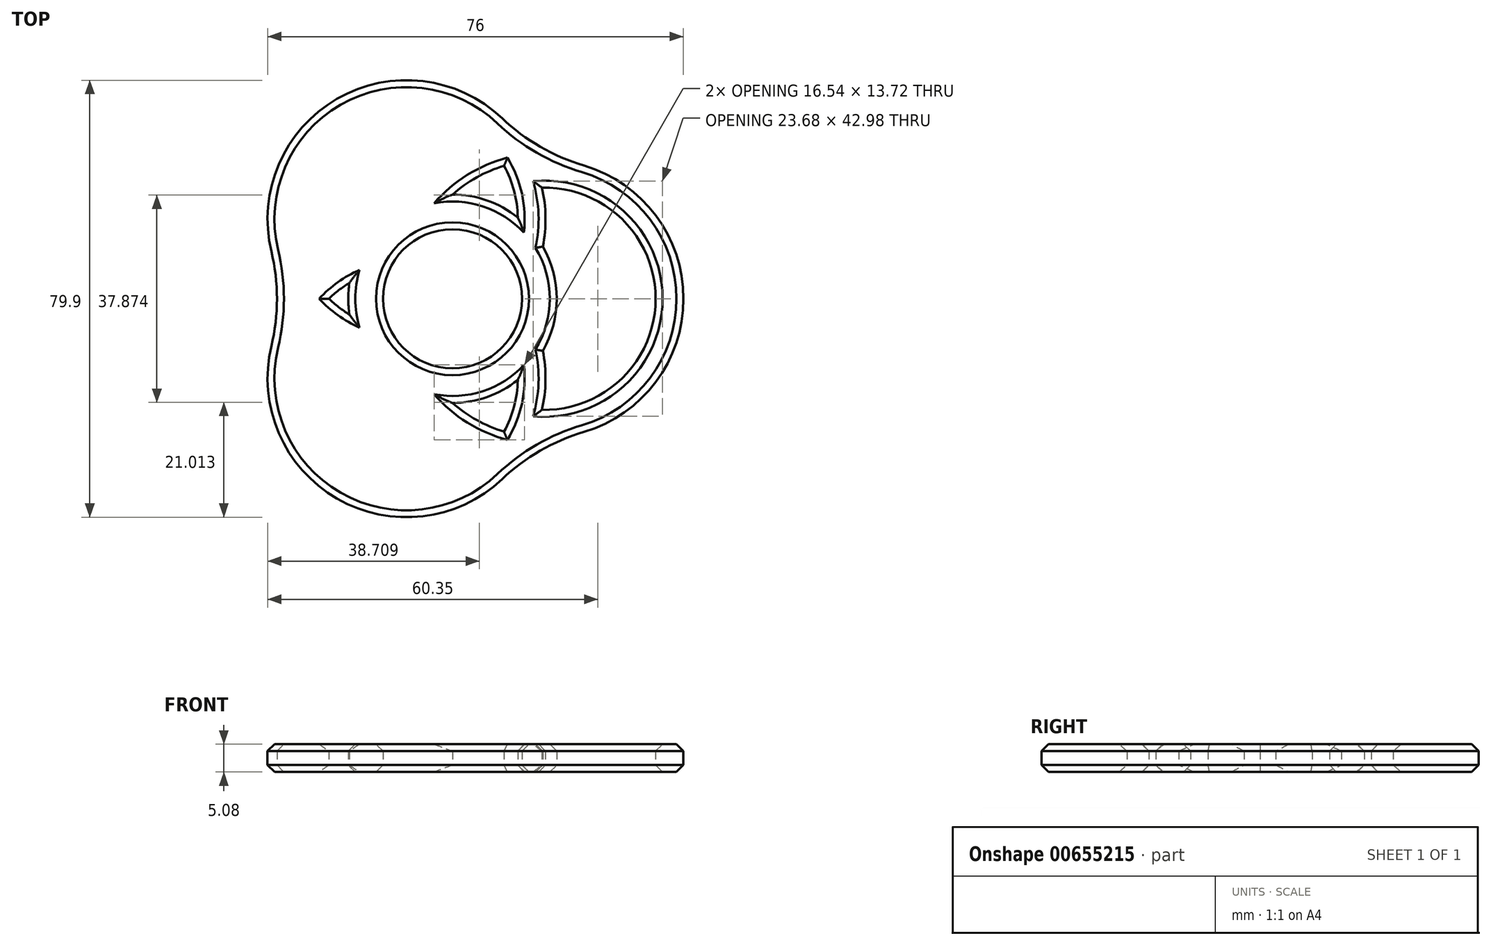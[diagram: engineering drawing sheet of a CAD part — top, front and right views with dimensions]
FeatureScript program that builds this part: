
annotation { "Feature Type Name" : "Feature", "Feature Type Description" : "" }
export const myFeature = defineFeature(function(context is Context, id is Id, definition is map)
    precondition{}
    {
        {
            var Q0;
            Q0=qCreatedBy(makeId("Top.planeOp"),FACE);
            var sketch = newSketch(context, id + "F0", { "sketchPlane" : qUnion([Q0])});
            skCircle(sketch, "E0", {"center": v(0, 0) * mm, "radius": 12.7 * mm});
            skCircle(sketch, "E1", {"center": v(0, 0) * mm, "radius": 19.05 * mm});
            skArc(sketch, "E2", {"start": v(0, -19.05) * mm, "mid": v(42.2, 0) * mm, "end": v(0, 19.05) * mm});
            skArc(sketch, "E3.0", {"start": v(2.5, -14.44) * mm, "mid": v(37.12, 0) * mm, "end": v(2.5, 14.44) * mm});
            skPoint(sketch, "E4.center", {"position": v(-0.02, -0.04) * mm});
            skArc(sketch, "E5.1.0", {"start": v(16.5, 9.53) * mm, "mid": v(-21.1, 36.55) * mm, "end": v(-16.5, -9.53) * mm});
            skArc(sketch, "E5.1.1", {"start": v(11.25, 9.39) * mm, "mid": v(-18.56, 32.15) * mm, "end": v(-13.76, -5.05) * mm});
            skArc(sketch, "E5.2.0", {"start": v(-16.5, 9.52) * mm, "mid": v(-21.1, -36.55) * mm, "end": v(16.5, -9.53) * mm});
            skArc(sketch, "E5.2.1", {"start": v(-13.76, 5.05) * mm, "mid": v(-18.56, -32.15) * mm, "end": v(11.25, -9.39) * mm});
            skArc(sketch, "E6", {"start": v(9.08, 32.97) * mm, "mid": v(16.04, 27.78) * mm, "end": v(24.02, 24.35) * mm});
            skArc(sketch, "E7.1.0", {"start": v(-33.1, -8.62) * mm, "mid": v(-32.08, 0) * mm, "end": v(-33.1, 8.62) * mm});
            skArc(sketch, "E7.2.0", {"start": v(24.02, -24.35) * mm, "mid": v(16.04, -27.78) * mm, "end": v(9.08, -32.97) * mm});
            skSolve(sketch);
        }
        {
            var Q0;
            Q0=qSketchRegion(id+"F0",true);
            var Q1;
            Q1=makeQuery(id+"F0.imprint","IMPRINT",FACE,{"disambiguationData":[TD([[makeQuery(id+"F0.imprint","IMPRINT",EDGE,{"derivedFrom":sQuery(id+"F0.wireOp",EDGE,"E0")}),-1.0]])]});
            var Q2;
            {var subQ0=sQuery(id+"F0.wireOp",EDGE,"E5.2.0");var subQ1=sQuery(id+"F0.wireOp",EDGE,"E1");var subQ2=makeQuery(id+"F0.imprint","INTERSECT",VERTEX,{"disambiguationData":[OD(1.0)],"derivedFrom":[subQ1,subQ0]});Q2=makeQuery(id+"F0.imprint","IMPRINT",FACE,{"disambiguationData":[TD([[makeQuery(id+"F0.imprint","IMPRINT",EDGE,{"disambiguationData":[TD([[subQ2,1.0]])],"derivedFrom":subQ1}),-1.0]])]});}
            var Q3;
            {var subQ0=sQuery(id+"F0.wireOp",EDGE,"E2");var subQ1=sQuery(id+"F0.wireOp",EDGE,"E1");var subQ2=makeQuery(id+"F0.imprint","INTERSECT",VERTEX,{"disambiguationData":[OD(0.0)],"derivedFrom":[subQ1,subQ0]});Q3=makeQuery(id+"F0.imprint","IMPRINT",FACE,{"disambiguationData":[TD([[makeQuery(id+"F0.imprint","IMPRINT",EDGE,{"disambiguationData":[TD([[subQ2,-1.0]])],"derivedFrom":subQ1}),-1.0]])]});}
            var Q4;
            {var subQ0=sQuery(id+"F0.wireOp",EDGE,"E5.2.1");var subQ1=sQuery(id+"F0.wireOp",EDGE,"E2");var subQ2=makeQuery(id+"F0.imprint","INTERSECT",VERTEX,{"derivedFrom":[subQ1,subQ0]});Q4=makeQuery(id+"F0.imprint","IMPRINT",FACE,{"disambiguationData":[TD([[makeQuery(id+"F0.imprint","IMPRINT",EDGE,{"disambiguationData":[TD([[subQ2,-1.0]])],"derivedFrom":subQ1}),1.0]])]});}
            var Q5;
            {var subQ0=sQuery(id+"F0.wireOp",EDGE,"E5.2.0");var subQ1=sQuery(id+"F0.wireOp",EDGE,"E1");var subQ2=makeQuery(id+"F0.imprint","INTERSECT",VERTEX,{"disambiguationData":[OD(0.0)],"derivedFrom":[subQ1,subQ0]});Q5=makeQuery(id+"F0.imprint","IMPRINT",FACE,{"disambiguationData":[TD([[makeQuery(id+"F0.imprint","IMPRINT",EDGE,{"disambiguationData":[TD([[subQ2,-1.0]])],"derivedFrom":subQ1}),-1.0]])]});}
            var Q6;
            {var subQ0=sQuery(id+"F0.wireOp",EDGE,"E5.2.0");var subQ1=sQuery(id+"F0.wireOp",EDGE,"E5.1.0");var subQ2=makeQuery(id+"F0.imprint","INTERSECT",VERTEX,{"derivedFrom":[subQ1,subQ0]});Q6=makeQuery(id+"F0.imprint","IMPRINT",FACE,{"disambiguationData":[TD([[makeQuery(id+"F0.imprint","IMPRINT",EDGE,{"disambiguationData":[TD([[subQ2,-1.0]])],"derivedFrom":subQ1}),1.0]])]});}
            var Q7;
            {var subQ0=sQuery(id+"F0.wireOp",EDGE,"E5.1.0");var subQ1=sQuery(id+"F0.wireOp",EDGE,"E1");var subQ2=makeQuery(id+"F0.imprint","INTERSECT",VERTEX,{"disambiguationData":[OD(1.0)],"derivedFrom":[subQ1,subQ0]});Q7=makeQuery(id+"F0.imprint","IMPRINT",FACE,{"disambiguationData":[TD([[makeQuery(id+"F0.imprint","IMPRINT",EDGE,{"disambiguationData":[TD([[subQ2,1.0]])],"derivedFrom":subQ1}),-1.0]])]});}
            var Q8;
            {var subQ0=sQuery(id+"F0.wireOp",EDGE,"E2");var subQ1=sQuery(id+"F0.wireOp",EDGE,"E1");var subQ2=makeQuery(id+"F0.imprint","INTERSECT",VERTEX,{"disambiguationData":[OD(1.0)],"derivedFrom":[subQ1,subQ0]});Q8=makeQuery(id+"F0.imprint","IMPRINT",FACE,{"disambiguationData":[TD([[makeQuery(id+"F0.imprint","IMPRINT",EDGE,{"disambiguationData":[TD([[subQ2,1.0]])],"derivedFrom":subQ1}),-1.0]])]});}
            var Q9;
            {var subQ0=sQuery(id+"F0.wireOp",EDGE,"E5.1.0");var subQ1=sQuery(id+"F0.wireOp",EDGE,"E1");var subQ2=makeQuery(id+"F0.imprint","INTERSECT",VERTEX,{"disambiguationData":[OD(0.0)],"derivedFrom":[subQ1,subQ0]});Q9=makeQuery(id+"F0.imprint","IMPRINT",FACE,{"disambiguationData":[TD([[makeQuery(id+"F0.imprint","IMPRINT",EDGE,{"disambiguationData":[TD([[subQ2,-1.0]])],"derivedFrom":subQ1}),-1.0]])]});}
            var Q10;
            {var subQ0=sQuery(id+"F0.wireOp",EDGE,"E5.1.0");var subQ1=sQuery(id+"F0.wireOp",EDGE,"E2");var subQ2=makeQuery(id+"F0.imprint","INTERSECT",VERTEX,{"derivedFrom":[subQ1,subQ0]});Q10=makeQuery(id+"F0.imprint","IMPRINT",FACE,{"disambiguationData":[TD([[makeQuery(id+"F0.imprint","IMPRINT",EDGE,{"disambiguationData":[TD([[subQ2,-1.0]])],"derivedFrom":subQ1}),1.0]])]});}
            extrude(context, id + "F1", {"entities" : qUnion([Q0, Q1, Q2, Q3, Q4, Q5, Q6, Q7, Q8, Q9, Q10]), "depth" : 5.08 * mm, "offsetDistance" : 25.4 * mm});
        }
        {
            var Q0;
            Q0=makeQuery(id+"F1.opExtrude","CAP_FACE",FACE,{"disambiguationData":[OSD([sQuery(id+"F0.wireOp",EDGE,"E0"),sQuery(id+"F0.wireOp",EDGE,"E1"),sQuery(id+"F0.wireOp",EDGE,"E2"),sQuery(id+"F0.wireOp",EDGE,"E3.0"),sQuery(id+"F0.wireOp",EDGE,"E5.1.0"),sQuery(id+"F0.wireOp",EDGE,"E5.1.1"),sQuery(id+"F0.wireOp",EDGE,"E5.2.0"),sQuery(id+"F0.wireOp",EDGE,"E5.2.1"),sQuery(id+"F0.wireOp",EDGE,"E6"),sQuery(id+"F0.wireOp",EDGE,"E7.1.0"),sQuery(id+"F0.wireOp",EDGE,"E7.2.0")])],"isStart":false});
            var Q1;
            Q1=makeQuery(id+"F1.opExtrude","CAP_FACE",FACE,{"disambiguationData":[OSD([sQuery(id+"F0.wireOp",EDGE,"E0"),sQuery(id+"F0.wireOp",EDGE,"E1"),sQuery(id+"F0.wireOp",EDGE,"E2"),sQuery(id+"F0.wireOp",EDGE,"E3.0"),sQuery(id+"F0.wireOp",EDGE,"E5.1.0"),sQuery(id+"F0.wireOp",EDGE,"E5.1.1"),sQuery(id+"F0.wireOp",EDGE,"E5.2.0"),sQuery(id+"F0.wireOp",EDGE,"E5.2.1"),sQuery(id+"F0.wireOp",EDGE,"E6"),sQuery(id+"F0.wireOp",EDGE,"E7.1.0"),sQuery(id+"F0.wireOp",EDGE,"E7.2.0")])],"isStart":true});
            chamfer(context, id + "F2", {"entities" : qUnion([Q0, Q1]), "width" : 1.27 * mm, "tangentPropagation" : true});
        }
    });
